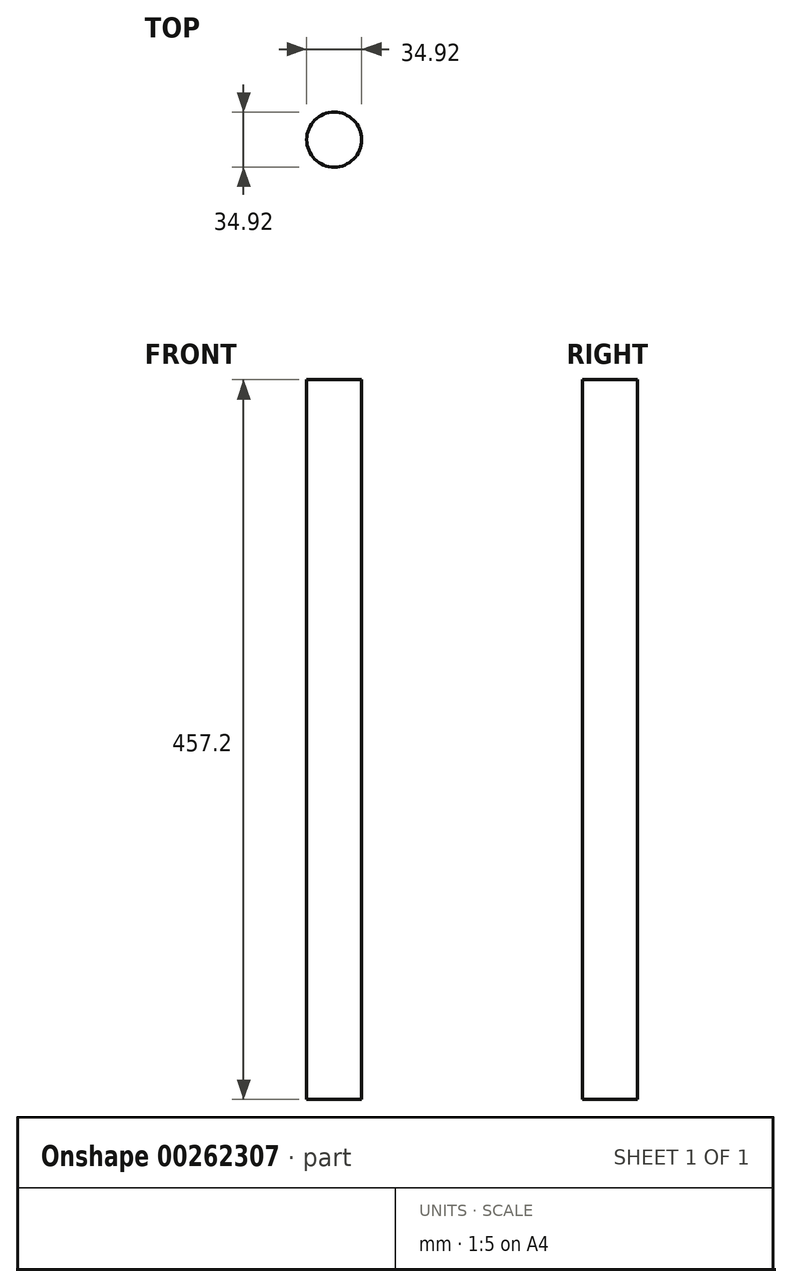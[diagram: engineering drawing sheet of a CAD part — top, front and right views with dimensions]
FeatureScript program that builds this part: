
annotation { "Feature Type Name" : "Feature", "Feature Type Description" : "" }
export const myFeature = defineFeature(function(context is Context, id is Id, definition is map)
    precondition{}
    {
        {
            var Q0;
            Q0=qCreatedBy(makeId("Front.planeOp"),FACE);
            var sketch = newSketch(context, id + "F0", { "sketchPlane" : qUnion([Q0])});
            skLineSegment(sketch, "E0", {"start": v(0, 0) * mm, "end": v(0, 152.4) * mm, "construction": true});
            skLineSegment(sketch, "E1", {"start": v(17.46, 152.4) * mm, "end": v(80.1, 152.4) * mm});
            skLineSegment(sketch, "E2", {"start": v(80.1, 152.4) * mm, "end": v(80.1, 130.5) * mm});
            skLineSegment(sketch, "E3", {"start": v(80.1, 130.5) * mm, "end": v(34.93, 115.6) * mm});
            skLineSegment(sketch, "E4", {"start": v(34.93, 115.6) * mm, "end": v(34.93, 100.73) * mm});
            skLineSegment(sketch, "E5", {"start": v(34.93, 100.73) * mm, "end": v(80.1, 100.73) * mm});
            skLineSegment(sketch, "E6", {"start": v(80.1, 100.73) * mm, "end": v(80.1, 81.06) * mm});
            skLineSegment(sketch, "E7", {"start": v(80.1, 81.06) * mm, "end": v(34.93, 61.93) * mm});
            skLineSegment(sketch, "E8", {"start": v(34.93, 61.93) * mm, "end": v(80.1, 30.57) * mm});
            skLineSegment(sketch, "E9", {"start": v(80.1, 30.57) * mm, "end": v(34.93, 0) * mm});
            skLineSegment(sketch, "E10", {"start": v(34.93, 0) * mm, "end": v(17.46, 0) * mm});
            skLineSegment(sketch, "E11", {"start": v(17.46, 0) * mm, "end": v(17.46, 152.4) * mm});
            skSolve(sketch);
        }
        {
            var Q0;
            Q0=qCreatedBy(makeId("Top.planeOp"),FACE);
            var sketch = newSketch(context, id + "F1", { "sketchPlane" : qUnion([Q0])});
            skPoint(sketch, "E12.0", {"position": v(17.46, 0) * mm});
            skCircle(sketch, "E13", {"center": v(0, 0) * mm, "radius": 17.46 * mm});
            skSolve(sketch);
        }
        {
            var Q0;
            Q0 = qSketchRegion(id + "F1", true);
            extrude(context, id + "F2", {"entities" : qUnion([Q0]), "endBound" : BoundingType.SYMMETRIC, "depth" : 457.2 * mm});
        }
    });
